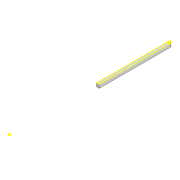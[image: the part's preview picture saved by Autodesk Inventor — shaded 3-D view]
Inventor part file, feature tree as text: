
AUTODESK INVENTOR PART (.ipt)
format: ipt  version: 2022 (Build 260153000, 153)  size: 109,568 bytes
history: native  units: mm
features: sketch x4, extrude x2, projected_geometry x2
ambient origin geometry x8: Origin, YZ Plane, XZ Plane, XY Plane, X Axis, Y Axis, Z Axis, Center Point
bodies: Solid1 (feature_tree)
feature tree (8):
  extrude  "Extrusion1"  Depth=6.0mm
  sketch  "Sketch2"  dims[d2=3.0mm d3=3.0mm]
  extrude  "Extrusion2"  Depth=3.0mm
  sketch  "Sketch4"  dims[d6=3.0mm d7=131.233mm d8=3.0mm d9=37.934mm d10=10.0mm d11=0.0mm]
  sketch  "Sketch1"  dims[d0=347.765mm d1=6.0mm]
  projected_geometry  "Projected Loop1"
  sketch  "Sketch3"  dims[d4=8.0mm d5=0.0mm]
  projected_geometry  "Projected Loop2"
